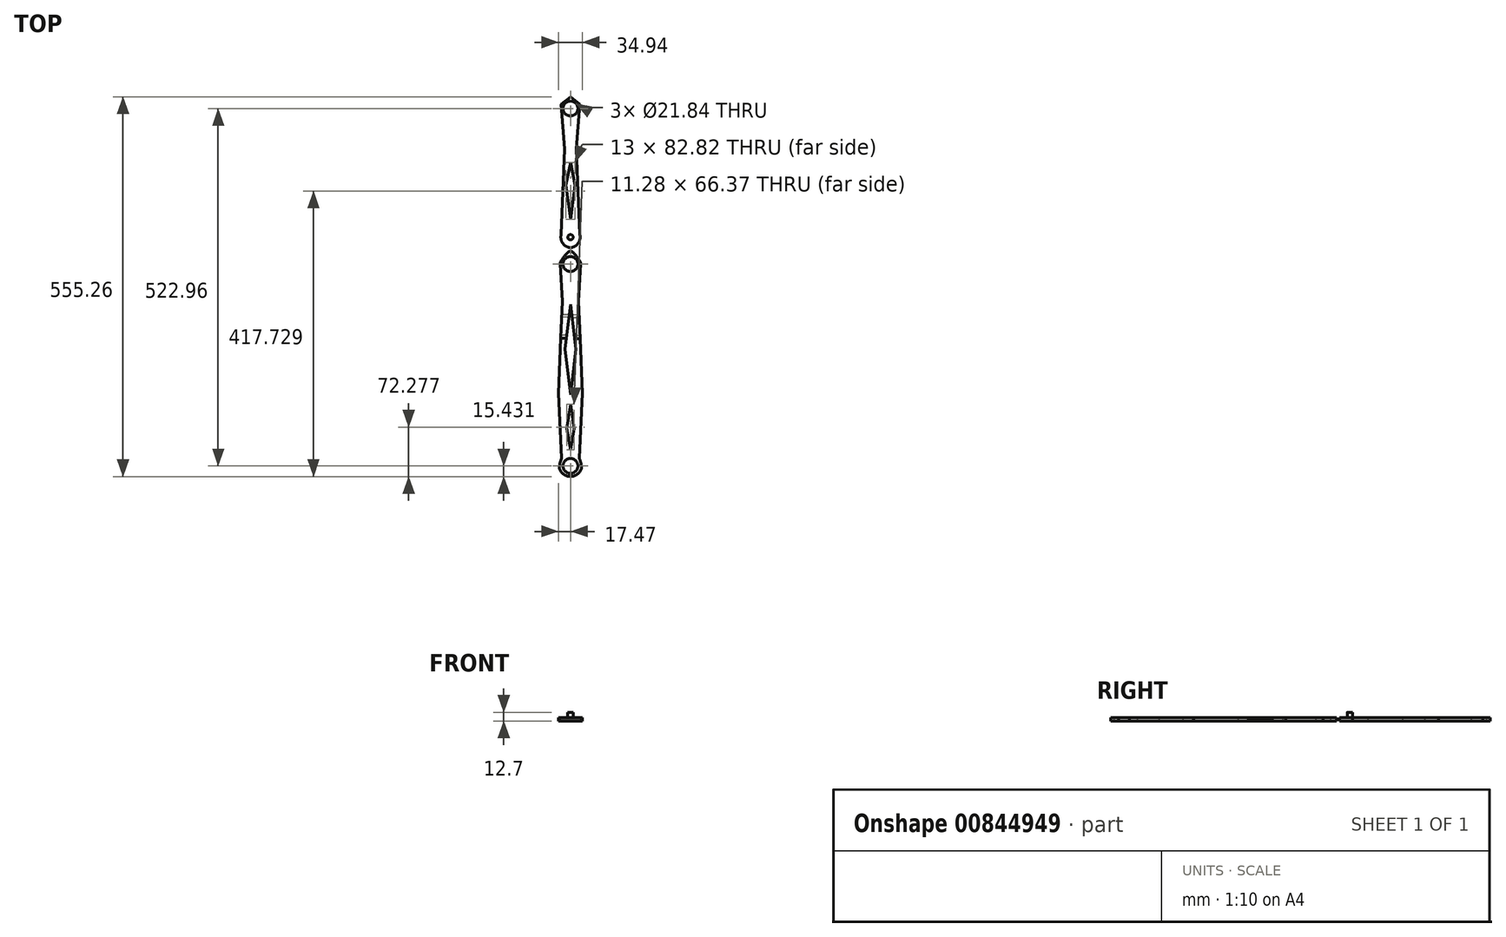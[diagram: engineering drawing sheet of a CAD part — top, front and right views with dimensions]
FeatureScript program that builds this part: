
annotation { "Feature Type Name" : "Feature", "Feature Type Description" : "" }
export const myFeature = defineFeature(function(context is Context, id is Id, definition is map)
    precondition{}
    {
        {
            var Q0;
            Q0=qCreatedBy(makeId("Top.planeOp"),FACE);
            var sketch = newSketch(context, id + "F0", { "sketchPlane" : qUnion([Q0])});
            skCircle(sketch, "E0", {"center": v(0, 0) * mm, "radius": 10.92 * mm});
            skArc(sketch, "E1", {"start": v(0, 19.28) * mm, "mid": v(-9.38, 11.06) * mm, "end": v(-15.12, 0) * mm});
            skLineSegment(sketch, "E2", {"start": v(0, 35.2) * mm, "end": v(0, -36.3) * mm});
            skArc(sketch, "E3.MirrorCS", {"start": v(0, 19.28) * mm, "mid": v(9.38, 11.06) * mm, "end": v(15.12, 0) * mm});
            skLineSegment(sketch, "E4", {"start": v(-15.12, 0) * mm, "end": v(-11.73, -54.6) * mm});
            skLineSegment(sketch, "E5.MirrorCS", {"start": v(15.12, 0) * mm, "end": v(11.73, -54.6) * mm});
            skPoint(sketch, "E6.end.orphan", {"position": v(-15.12, -320.54) * mm});
            skPoint(sketch, "E7.end.orphan", {"position": v(-31.77, -227.13) * mm});
            skLineSegment(sketch, "E8", {"start": v(-11.73, -54.6) * mm, "end": v(-17.47, -189.47) * mm});
            skPoint(sketch, "E9.MirrorCS.end.orphan", {"position": v(31.77, -227.13) * mm});
            skPoint(sketch, "E9.MirrorCS.start.orphan", {"position": v(11.73, -54.6) * mm});
            skPoint(sketch, "E10.MirrorCS.end.orphan", {"position": v(15.12, -320.54) * mm});
            skLineSegment(sketch, "E11", {"start": v(-17.47, -189.47) * mm, "end": v(-12.87, -283.68) * mm});
            skLineSegment(sketch, "E12.MirrorCS", {"start": v(11.73, -54.6) * mm, "end": v(17.47, -189.47) * mm});
            skLineSegment(sketch, "E13.MirrorCS", {"start": v(17.47, -189.47) * mm, "end": v(12.87, -283.68) * mm});
            skCircle(sketch, "E14", {"center": v(0, -295.43) * mm, "radius": 10.92 * mm});
            skLineSegment(sketch, "E15", {"start": v(0, -59.29) * mm, "end": v(-7.96, -124.44) * mm});
            skLineSegment(sketch, "E16", {"start": v(-7.96, -124.44) * mm, "end": v(0, -191.1) * mm});
            skLineSegment(sketch, "E17.MirrorCS", {"start": v(0, -59.29) * mm, "end": v(7.96, -124.44) * mm});
            skLineSegment(sketch, "E18.MirrorCS", {"start": v(7.96, -124.44) * mm, "end": v(0, -191.1) * mm});
            skLineSegment(sketch, "E19", {"start": v(0, -205.4) * mm, "end": v(-5.64, -240.4) * mm});
            skLineSegment(sketch, "E20", {"start": v(-5.64, -240.4) * mm, "end": v(0, -271.77) * mm});
            skLineSegment(sketch, "E21.MirrorCS", {"start": v(0, -205.4) * mm, "end": v(5.64, -240.4) * mm});
            skLineSegment(sketch, "E22.MirrorCS", {"start": v(5.64, -240.4) * mm, "end": v(0, -271.77) * mm});
            skArc(sketch, "E23", {"start": v(-12.87, -283.68) * mm, "mid": v(-15.27, -291.3) * mm, "end": v(-16.08, -299.25) * mm});
            skArc(sketch, "E24.MirrorCS", {"start": v(12.87, -283.68) * mm, "mid": v(15.27, -291.3) * mm, "end": v(16.08, -299.25) * mm});
            skArc(sketch, "E25", {"start": v(-16.08, -299.25) * mm, "mid": v(0, -310.86) * mm, "end": v(16.08, -299.25) * mm});
            skPoint(sketch, "E26.start.orphan", {"position": v(-12.87, -314.82) * mm});
            skPoint(sketch, "E27.orphan", {"position": v(12.87, -314.82) * mm});
            skPoint(sketch, "E28.MirrorCS.start.orphan", {"position": v(12.87, -283.68) * mm});
            skSolve(sketch);
        }
        {
            var Q0;
            Q0 = qSketchRegion(id + "F0", true);
            extrude(context, id + "F1", {"entities" : qUnion([Q0]), "depth" : 5.08 * mm, "offsetDistance" : 25.4 * mm});
        }
        {
            var Q0;
            Q0=makeQuery(id+"F1.opExtrude","SWEPT_FACE",FACE,{"disambiguationData":[OSD([sQuery(id+"F0.wireOp",EDGE,"E8")])]});
            var sketch = newSketch(context, id + "F2", { "sketchPlane" : qUnion([Q0])});
            skLineSegment(sketch, "E29", {"start": v(108.5, 5.08) * mm, "end": v(108.5, 1.5) * mm});
            skLineSegment(sketch, "E30", {"start": v(108.5, 1.5) * mm, "end": v(104.58, 1.5) * mm});
            skLineSegment(sketch, "E31", {"start": v(104.58, 1.5) * mm, "end": v(104.58, 2.65) * mm});
            skLineSegment(sketch, "E32", {"start": v(104.58, 2.65) * mm, "end": v(78.26, 2.65) * mm});
            skLineSegment(sketch, "E33", {"start": v(78.26, 2.65) * mm, "end": v(78.26, 3.74) * mm});
            skLineSegment(sketch, "E34", {"start": v(78.26, 3.74) * mm, "end": v(74.09, 3.74) * mm});
            skLineSegment(sketch, "E35", {"start": v(74.09, 3.74) * mm, "end": v(74.09, 0) * mm});
            skLineSegment(sketch, "E36", {"start": v(74.09, 0) * mm, "end": v(74.3, 0) * mm});
            skLineSegment(sketch, "E37", {"start": v(108.64, 5.08) * mm, "end": v(108.5, 5.08) * mm});
            skPoint(sketch, "E38.start.orphan", {"position": v(74.3, 2.55) * mm});
            skPoint(sketch, "E39.end.orphan", {"position": v(78.1, 2.55) * mm});
            skLineSegment(sketch, "E40", {"start": v(74.45, 0) * mm, "end": v(74.45, 3.36) * mm});
            skLineSegment(sketch, "E41", {"start": v(74.45, 3.36) * mm, "end": v(78, 3.36) * mm});
            skLineSegment(sketch, "E42", {"start": v(78, 3.36) * mm, "end": v(78, 2.37) * mm});
            skLineSegment(sketch, "E43", {"start": v(78, 2.37) * mm, "end": v(104.25, 2.37) * mm});
            skLineSegment(sketch, "E44", {"start": v(104.25, 2.37) * mm, "end": v(104.25, 1.15) * mm});
            skLineSegment(sketch, "E45", {"start": v(104.25, 1.15) * mm, "end": v(108.78, 1.15) * mm});
            skLineSegment(sketch, "E46", {"start": v(108.78, 1.15) * mm, "end": v(108.78, 5.08) * mm});
            skLineSegment(sketch, "E47", {"start": v(74.45, 0) * mm, "end": v(74.09, 0) * mm});
            skLineSegment(sketch, "E48", {"start": v(108.78, 5.08) * mm, "end": v(108.5, 5.08) * mm});
            skSolve(sketch);
        }
        {
            var Q0;
            Q0=qCreatedBy(makeId("Top.planeOp"),FACE);
            var sketch = newSketch(context, id + "F3", { "sketchPlane" : qUnion([Q0])});
            skArc(sketch, "E49", {"start": v(-13.66, 43.13) * mm, "mid": v(-11.27, 30.33) * mm, "end": v(0, 23.8) * mm});
            skLineSegment(sketch, "E50", {"start": v(0, 23.8) * mm, "end": v(0, 95.8) * mm});
            skArc(sketch, "E51.MirrorCS", {"start": v(13.66, 43.13) * mm, "mid": v(11.27, 30.33) * mm, "end": v(0, 23.8) * mm});
            skLineSegment(sketch, "E52", {"start": v(-13.66, 43.13) * mm, "end": v(-8.83, 168.53) * mm});
            skLineSegment(sketch, "E53", {"start": v(-8.83, 168.53) * mm, "end": v(-13.66, 233.56) * mm});
            skLineSegment(sketch, "E54", {"start": v(-13.66, 233.56) * mm, "end": v(0, 244.4) * mm});
            skLineSegment(sketch, "E55.MirrorCS", {"start": v(13.66, 43.13) * mm, "end": v(8.83, 168.53) * mm});
            skLineSegment(sketch, "E56.MirrorCS", {"start": v(8.83, 168.53) * mm, "end": v(13.66, 233.56) * mm});
            skLineSegment(sketch, "E57.MirrorCS", {"start": v(13.66, 233.56) * mm, "end": v(0, 244.4) * mm});
            skLineSegment(sketch, "E58", {"start": v(0, 65.46) * mm, "end": v(-6.5, 115.78) * mm});
            skLineSegment(sketch, "E59", {"start": v(-6.5, 115.78) * mm, "end": v(0, 148.28) * mm});
            skLineSegment(sketch, "E60.MirrorCS", {"start": v(0, 65.46) * mm, "end": v(6.5, 115.78) * mm});
            skLineSegment(sketch, "E61.MirrorCS", {"start": v(6.5, 115.78) * mm, "end": v(0, 148.28) * mm});
            skCircle(sketch, "E62", {"center": v(0, 227.53) * mm, "radius": 10.92 * mm});
            skPoint(sketch, "E63.center.orphan", {"position": v(0, 39.21) * mm});
            skCircle(sketch, "E64", {"center": v(0, 39.21) * mm, "radius": 3.91 * mm});
            skSolve(sketch);
        }
        {
            var Q0;
            Q0 = qSketchRegion(id + "F3", true);
            extrude(context, id + "F4", {"entities" : qUnion([Q0]), "depth" : 5.08 * mm, "offsetDistance" : 25.4 * mm});
        }
        {
            var Q0;
            {var subQ0=sQuery(id+"F3.wireOp",EDGE,"E64");var subQ1=sQuery(id+"F3.wireOp",EDGE,"E50");var subQ2=makeQuery(id+"F3.imprint","INTERSECT",VERTEX,{"disambiguationData":[OD(0.0)],"derivedFrom":[subQ1,subQ0]});Q0=makeQuery(id+"F3.imprint","IMPRINT",FACE,{"disambiguationData":[TD([[makeQuery(id+"F3.imprint","IMPRINT",EDGE,{"disambiguationData":[TD([[subQ2,-1.0]])],"derivedFrom":subQ1}),1.0]])]});}
            var Q1;
            {var subQ0=sQuery(id+"F3.wireOp",EDGE,"E64");var subQ1=sQuery(id+"F3.wireOp",EDGE,"E50");var subQ2=makeQuery(id+"F3.imprint","INTERSECT",VERTEX,{"disambiguationData":[OD(0.0)],"derivedFrom":[subQ1,subQ0]});Q1=makeQuery(id+"F3.imprint","IMPRINT",FACE,{"disambiguationData":[TD([[makeQuery(id+"F3.imprint","IMPRINT",EDGE,{"disambiguationData":[TD([[subQ2,-1.0]])],"derivedFrom":subQ1}),-1.0]])]});}
            extrude(context, id + "F5", {"entities" : qUnion([Q0, Q1]), "operationType" : NewBodyOperationType.ADD, "depth" : 12.7 * mm, "offsetDistance" : 25.4 * mm});
        }
        {
            var Q0;
            Q0 = qSketchRegion(id + "F2", true);
            var Q1;
            Q1=makeQuery(id+"F1.opExtrude","SWEPT_FACE",FACE,{"disambiguationData":[OSD([sQuery(id+"F0.wireOp",EDGE,"E12.MirrorCS")])]});
            extrude(context, id + "F6", {"entities" : qUnion([Q0, Q1]), "operationType" : NewBodyOperationType.REMOVE, "endBound" : BoundingType.THROUGH_ALL, "oppositeDirection" : true, "depth" : 25.4 * mm, "offsetDistance" : 25.4 * mm});
        }
    });
